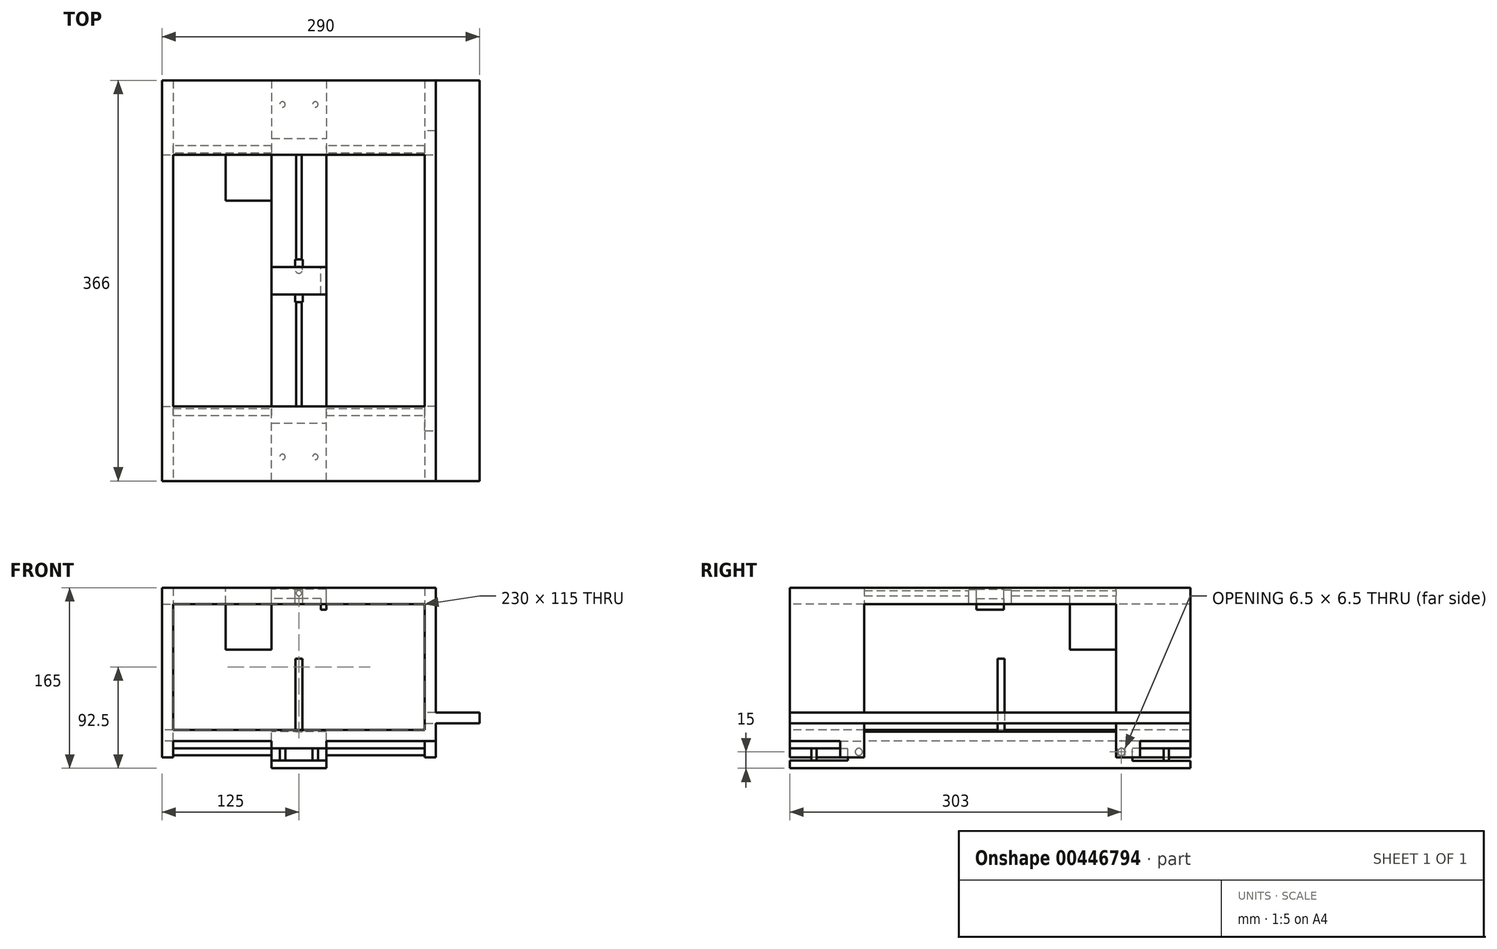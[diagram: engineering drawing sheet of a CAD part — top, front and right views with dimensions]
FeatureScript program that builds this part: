
annotation { "Feature Type Name" : "Feature", "Feature Type Description" : "" }
export const myFeature = defineFeature(function(context is Context, id is Id, definition is map)
    precondition{}
    {
        {
            var Q0;
            Q0=qCreatedBy(makeId("Top.planeOp"),FACE);
            var sketch = newSketch(context, id + "F0", { "sketchPlane" : qUnion([Q0])});
            skLineSegment(sketch, "E0.bottom", {"start": v(-125, 125) * mm, "end": v(125, 125) * mm});
            skLineSegment(sketch, "E0.top", {"start": v(-125, -125) * mm, "end": v(125, -125) * mm});
            skLineSegment(sketch, "E0.left", {"start": v(-125, 125) * mm, "end": v(-125, -125) * mm});
            skLineSegment(sketch, "E0.right", {"start": v(125, 125) * mm, "end": v(125, -125) * mm});
            skSolve(sketch);
        }
        {
            var Q0;
            Q0=qSketchRegion(id+"F0",true);
            extrude(context, id + "F1", {"entities" : qUnion([Q0]), "endBound" : BoundingType.SYMMETRIC, "depth" : 140 * mm});
        }
        {
            var Q0;
            Q0=makeQuery(id+"F1.opExtrude","CAP_FACE",FACE,{"disambiguationData":[OSD([sQuery(id+"F0.wireOp",EDGE,"E0.bottom"),sQuery(id+"F0.wireOp",EDGE,"E0.top"),sQuery(id+"F0.wireOp",EDGE,"E0.left"),sQuery(id+"F0.wireOp",EDGE,"E0.right")])],"isStart":false});
            shell(context, id + "F2", {"entities" : qUnion([Q0]), "thickness" : 10 * mm});
        }
        {
            var Q0;
            Q0=makeQuery(id+"F1.opExtrude","SWEPT_FACE",FACE,{"disambiguationData":[OSD([sQuery(id+"F0.wireOp",EDGE,"E0.top")])]});
            var sketch = newSketch(context, id + "F3", { "sketchPlane" : qUnion([Q0])});
            skLineSegment(sketch, "E1.bottom", {"start": v(-115, 60) * mm, "end": v(115, 60) * mm});
            skLineSegment(sketch, "E1.top", {"start": v(-115, -60) * mm, "end": v(115, -60) * mm});
            skLineSegment(sketch, "E1.left", {"start": v(-115, 60) * mm, "end": v(-115, -60) * mm});
            skLineSegment(sketch, "E1.right", {"start": v(115, 60) * mm, "end": v(115, -60) * mm});
            skSolve(sketch);
        }
        {
            var Q0;
            Q0=makeQuery(id+"F3.imprint","IMPRINT",FACE,{"disambiguationData":[TD([[makeQuery(id+"F3.imprint","IMPRINT",EDGE,{"derivedFrom":sQuery(id+"F3.wireOp",EDGE,"E1.bottom")}),-1.0]])]});
            extrude(context, id + "F4", {"entities" : qUnion([Q0]), "operationType" : NewBodyOperationType.REMOVE, "oppositeDirection" : true, "depth" : 300 * mm});
        }
        {
            var Q0;
            Q0=makeQuery(id+"F1.opExtrude","SWEPT_FACE",FACE,{"disambiguationData":[OSD([sQuery(id+"F0.wireOp",EDGE,"E0.left")])]});
            var sketch = newSketch(context, id + "F5", { "sketchPlane" : qUnion([Q0])});
            skLineSegment(sketch, "E2.bottom", {"start": v(115, 60) * mm, "end": v(-115, 60) * mm});
            skLineSegment(sketch, "E2.top", {"start": v(115, -60) * mm, "end": v(-115, -60) * mm});
            skLineSegment(sketch, "E2.left", {"start": v(115, 60) * mm, "end": v(115, -60) * mm});
            skLineSegment(sketch, "E2.right", {"start": v(-115, 60) * mm, "end": v(-115, -60) * mm});
            skSolve(sketch);
        }
        {
            var Q0;
            Q0=makeQuery(id+"F5.imprint","IMPRINT",FACE,{"disambiguationData":[TD([[makeQuery(id+"F5.imprint","IMPRINT",EDGE,{"derivedFrom":sQuery(id+"F5.wireOp",EDGE,"E2.bottom")}),1.0]])]});
            extrude(context, id + "F6", {"entities" : qUnion([Q0]), "operationType" : NewBodyOperationType.REMOVE, "oppositeDirection" : true, "depth" : 300 * mm});
        }
        {
            var Q0;
            Q0=makeQuery(id+"F6.boolean.opBoolean","MERGE",FACE,{"derivedFrom":[makeQuery(id+"F4.boolean.opBoolean","MERGE",FACE,{"derivedFrom":[makeQuery(id+"F2.opShell","OFFSET_FACE",FACE,{"disambiguationData":[OSD([sQuery(id+"F0.wireOp",EDGE,"E0.bottom"),sQuery(id+"F0.wireOp",EDGE,"E0.top"),sQuery(id+"F0.wireOp",EDGE,"E0.left"),sQuery(id+"F0.wireOp",EDGE,"E0.right")])]}),makeQuery(id+"F4.opExtrude","SWEPT_FACE",FACE,{"disambiguationData":[OSD([sQuery(id+"F3.wireOp",EDGE,"E1.top")])]})]}),makeQuery(id+"F6.opExtrude","SWEPT_FACE",FACE,{"disambiguationData":[OSD([sQuery(id+"F5.wireOp",EDGE,"E2.top")])]})]});
            var sketch = newSketch(context, id + "F7", { "sketchPlane" : qUnion([Q0])});
            skLineSegment(sketch, "E3.bottom", {"start": v(-115, 115) * mm, "end": v(115, 115) * mm});
            skLineSegment(sketch, "E3.top", {"start": v(-115, -115) * mm, "end": v(115, -115) * mm});
            skLineSegment(sketch, "E3.left", {"start": v(-115, 115) * mm, "end": v(-115, -115) * mm});
            skLineSegment(sketch, "E3.right", {"start": v(115, 115) * mm, "end": v(115, -115) * mm});
            skSolve(sketch);
        }
        {
            var Q0;
            Q0=makeQuery(id+"F7.imprint","IMPRINT",FACE,{"disambiguationData":[TD([[makeQuery(id+"F7.imprint","IMPRINT",EDGE,{"derivedFrom":sQuery(id+"F7.wireOp",EDGE,"E3.bottom")}),-1.0]])]});
            extrude(context, id + "F8", {"entities" : qUnion([Q0]), "operationType" : NewBodyOperationType.REMOVE, "oppositeDirection" : true, "depth" : 500 * mm});
        }
        {
            var Q0;
            Q0=makeQuery(id+"F1.opExtrude","CAP_FACE",FACE,{"disambiguationData":[OSD([sQuery(id+"F0.wireOp",EDGE,"E0.bottom"),sQuery(id+"F0.wireOp",EDGE,"E0.top"),sQuery(id+"F0.wireOp",EDGE,"E0.left"),sQuery(id+"F0.wireOp",EDGE,"E0.right")])],"isStart":true});
            var sketch = newSketch(context, id + "F9", { "sketchPlane" : qUnion([Q0])});
            skLineSegment(sketch, "E4.bottom", {"start": v(-125, -125) * mm, "end": v(-115, -125) * mm});
            skLineSegment(sketch, "E4.top", {"start": v(-125, -115) * mm, "end": v(-115, -115) * mm});
            skLineSegment(sketch, "E4.left", {"start": v(-125, -125) * mm, "end": v(-125, -115) * mm});
            skLineSegment(sketch, "E4.right", {"start": v(-115, -125) * mm, "end": v(-115, -115) * mm});
            skLineSegment(sketch, "E5.bottom", {"start": v(-115, 115) * mm, "end": v(-125, 115) * mm});
            skLineSegment(sketch, "E5.top", {"start": v(-115, 125) * mm, "end": v(-125, 125) * mm});
            skLineSegment(sketch, "E5.left", {"start": v(-115, 115) * mm, "end": v(-115, 125) * mm});
            skLineSegment(sketch, "E5.right", {"start": v(-125, 115) * mm, "end": v(-125, 125) * mm});
            skLineSegment(sketch, "E6.bottom", {"start": v(125, -125) * mm, "end": v(115, -125) * mm});
            skLineSegment(sketch, "E6.top", {"start": v(125, -115) * mm, "end": v(115, -115) * mm});
            skLineSegment(sketch, "E6.left", {"start": v(125, -125) * mm, "end": v(125, -115) * mm});
            skLineSegment(sketch, "E6.right", {"start": v(115, -125) * mm, "end": v(115, -115) * mm});
            skLineSegment(sketch, "E7.bottom", {"start": v(125, 125) * mm, "end": v(115, 125) * mm});
            skLineSegment(sketch, "E7.top", {"start": v(125, 115) * mm, "end": v(115, 115) * mm});
            skLineSegment(sketch, "E7.left", {"start": v(125, 125) * mm, "end": v(125, 115) * mm});
            skLineSegment(sketch, "E7.right", {"start": v(115, 125) * mm, "end": v(115, 115) * mm});
            skSolve(sketch);
        }
        {
            var Q0;
            Q0=qSketchRegion(id+"F9",true);
            var Q1;
            Q1=makeQuery(id+"F1.opExtrude","CAP_FACE",FACE,{"disambiguationData":[OSD([sQuery(id+"F0.wireOp",EDGE,"E0.bottom"),sQuery(id+"F0.wireOp",EDGE,"E0.top"),sQuery(id+"F0.wireOp",EDGE,"E0.left"),sQuery(id+"F0.wireOp",EDGE,"E0.right")])],"isStart":false});
            extrude(context, id + "F10", {"entities" : qUnion([Q0, Q1]), "operationType" : NewBodyOperationType.ADD, "depth" : 15 * mm});
        }
        {
            var Q0;
            Q0=makeQuery(id+"F10.boolean.opBoolean","MERGE",FACE,{"derivedFrom":[makeQuery(id+"F1.opExtrude","SWEPT_FACE",FACE,{"disambiguationData":[OSD([sQuery(id+"F0.wireOp",EDGE,"E0.bottom")])]}),makeQuery(id+"F10.opExtrude","SWEPT_FACE",FACE,{"disambiguationData":[OSD([sQuery(id+"F9.wireOp",EDGE,"E4.bottom")])]}),makeQuery(id+"F10.opExtrude","SWEPT_FACE",FACE,{"disambiguationData":[OSD([sQuery(id+"F9.wireOp",EDGE,"E6.bottom")])]})]});
            var sketch = newSketch(context, id + "F11", { "sketchPlane" : qUnion([Q0])});
            skCircle(sketch, "E8", {"center": v(0, 65) * mm, "radius": 2.5 * mm});
            skSolve(sketch);
        }
        {
            var Q0;
            Q0=qSketchRegion(id+"F11",true);
            extrude(context, id + "F12", {"entities" : qUnion([Q0]), "operationType" : NewBodyOperationType.ADD, "oppositeDirection" : true, "depth" : 250 * mm});
        }
        {
            var Q0;
            Q0=qCreatedBy(makeId("Front.planeOp"),FACE);
            var sketch = newSketch(context, id + "F13", { "sketchPlane" : qUnion([Q0])});
            skLineSegment(sketch, "E9.bottom", {"start": v(25, 50) * mm, "end": v(-25, 50) * mm});
            skLineSegment(sketch, "E9.top", {"start": v(25, 68.5) * mm, "end": v(-25, 68.5) * mm});
            skLineSegment(sketch, "E9.left", {"start": v(25, 50) * mm, "end": v(25, 68.5) * mm});
            skLineSegment(sketch, "E9.right", {"start": v(-25, 50) * mm, "end": v(-25, 68.5) * mm});
            skSolve(sketch);
        }
        {
            var Q0;
            Q0=qSketchRegion(id+"F13",true);
            extrude(context, id + "F14", {"entities" : qUnion([Q0]), "operationType" : NewBodyOperationType.ADD, "endBound" : BoundingType.SYMMETRIC, "depth" : 25 * mm});
        }
        {
            var Q0;
            Q0=makeQuery(id+"F14.opExtrude","SWEPT_FACE",FACE,{"disambiguationData":[OSD([sQuery(id+"F13.wireOp",EDGE,"E9.bottom")])]});
            var sketch = newSketch(context, id + "F15", { "sketchPlane" : qUnion([Q0])});
            skLineSegment(sketch, "E10.right", {"start": v(20, 7.5) * mm, "end": v(20, -12.5) * mm});
            skLineSegment(sketch, "E11", {"start": v(20, 7.5) * mm, "end": v(20, 12.5) * mm});
            skLineSegment(sketch, "E12", {"start": v(20, 12.5) * mm, "end": v(25, 12.5) * mm});
            skLineSegment(sketch, "E13", {"start": v(25, 12.5) * mm, "end": v(25, -12.5) * mm});
            skLineSegment(sketch, "E14", {"start": v(25, -12.5) * mm, "end": v(20, -12.5) * mm});
            skSolve(sketch);
        }
        {
            var Q0;
            {var subQ3=sQuery(id+"F15.wireOp",EDGE,"E10.right");Q0=makeQuery(id+"F15.imprint","IMPRINT",FACE,{"disambiguationData":[TD([[makeQuery(id+"F15.imprint","IMPRINT",EDGE,{"derivedFrom":subQ3}),-1.0]])]});}
            extrude(context, id + "F16", {"entities" : qUnion([Q0]), "operationType" : NewBodyOperationType.REMOVE, "oppositeDirection" : true, "depth" : 10 * mm});
        }
        {
            var Q0;
            Q0=qCreatedBy(makeId("Right.planeOp"),FACE);
            var sketch = newSketch(context, id + "F17", { "sketchPlane" : qUnion([Q0])});
            skLineSegment(sketch, "E15.bottom", {"start": v(-12.5, 55) * mm, "end": v(-19.5, 55) * mm});
            skLineSegment(sketch, "E15.top", {"start": v(-12.5, 68) * mm, "end": v(-19.5, 68) * mm});
            skLineSegment(sketch, "E15.left", {"start": v(-12.5, 55) * mm, "end": v(-12.5, 68) * mm});
            skLineSegment(sketch, "E15.right", {"start": v(-19.5, 55) * mm, "end": v(-19.5, 68) * mm});
            skLineSegment(sketch, "E16.bottom", {"start": v(12.5, 55) * mm, "end": v(19.5, 55) * mm});
            skLineSegment(sketch, "E16.top", {"start": v(12.5, 68) * mm, "end": v(19.5, 68) * mm});
            skLineSegment(sketch, "E16.left", {"start": v(12.5, 55) * mm, "end": v(12.5, 68) * mm});
            skLineSegment(sketch, "E16.right", {"start": v(19.5, 55) * mm, "end": v(19.5, 68) * mm});
            skSolve(sketch);
        }
        {
            var Q0;
            Q0=qSketchRegion(id+"F17",true);
            extrude(context, id + "F18", {"entities" : qUnion([Q0]), "operationType" : NewBodyOperationType.ADD, "endBound" : BoundingType.SYMMETRIC, "depth" : 7 * mm});
        }
        {
            var Q0;
            Q0=makeQuery(id+"F10.opExtrude","SWEPT_FACE",FACE,{"disambiguationData":[OSD([sQuery(id+"F9.wireOp",EDGE,"E4.right")])]});
            var sketch = newSketch(context, id + "F19", { "sketchPlane" : qUnion([Q0])});
            skCircle(sketch, "E17", {"center": v(120, -80) * mm, "radius": 3.25 * mm});
            skSolve(sketch);
        }
        {
            var Q0;
            Q0=qSketchRegion(id+"F19",true);
            extrude(context, id + "F20", {"entities" : qUnion([Q0]), "operationType" : NewBodyOperationType.ADD, "depth" : 240 * mm});
        }
        {
            var Q0;
            Q0=qCreatedBy(makeId("Front.planeOp"),FACE);
            var sketch = newSketch(context, id + "F21", { "sketchPlane" : qUnion([Q0])});
            skLineSegment(sketch, "E18.bottom", {"start": v(25, -95) * mm, "end": v(-25, -95) * mm});
            skLineSegment(sketch, "E18.top", {"start": v(25, -61.69) * mm, "end": v(-25, -61.69) * mm});
            skLineSegment(sketch, "E18.left", {"start": v(25, -95) * mm, "end": v(25, -61.69) * mm});
            skLineSegment(sketch, "E18.right", {"start": v(-25, -95) * mm, "end": v(-25, -61.69) * mm});
            skSolve(sketch);
        }
        {
            var Q0;
            Q0=makeQuery(id+"F21.imprint","IMPRINT",FACE,{"disambiguationData":[TD([[makeQuery(id+"F21.imprint","IMPRINT",EDGE,{"derivedFrom":sQuery(id+"F21.wireOp",EDGE,"E18.bottom")}),-1.0]])]});
            extrude(context, id + "F22", {"entities" : qUnion([Q0]), "operationType" : NewBodyOperationType.ADD, "endBound" : BoundingType.SYMMETRIC, "depth" : 230 * mm});
        }
        {
            var Q0;
            Q0=makeQuery(id+"F10.opExtrude","SWEPT_FACE",FACE,{"disambiguationData":[OSD([sQuery(id+"F9.wireOp",EDGE,"E7.right")])]});
            var sketch = newSketch(context, id + "F23", { "sketchPlane" : qUnion([Q0])});
            skCircle(sketch, "E19", {"center": v(120, -80) * mm, "radius": 3.25 * mm});
            skSolve(sketch);
        }
        {
            var Q0;
            Q0=makeQuery(id+"F23.imprint","IMPRINT",FACE,{"disambiguationData":[TD([[makeQuery(id+"F23.imprint","IMPRINT",EDGE,{"derivedFrom":sQuery(id+"F23.wireOp",EDGE,"E19")}),1.0]])]});
            extrude(context, id + "F24", {"entities" : qUnion([Q0]), "operationType" : NewBodyOperationType.ADD, "depth" : 240 * mm});
        }
        {
            var Q0;
            Q0=makeQuery(id+"F22.opExtrude","SWEPT_FACE",FACE,{"disambiguationData":[OSD([sQuery(id+"F21.wireOp",EDGE,"E18.bottom")])]});
            var sketch = newSketch(context, id + "F25", { "sketchPlane" : qUnion([Q0])});
            skCircle(sketch, "E20", {"center": v(0, -10) * mm, "radius": 3.25 * mm});
            skSolve(sketch);
        }
        {
            var Q0;
            Q0=makeQuery(id+"F25.imprint","IMPRINT",FACE,{"disambiguationData":[TD([[makeQuery(id+"F25.imprint","IMPRINT",EDGE,{"derivedFrom":sQuery(id+"F25.wireOp",EDGE,"E20")}),1.0]])]});
            extrude(context, id + "F26", {"entities" : qUnion([Q0]), "operationType" : NewBodyOperationType.ADD, "oppositeDirection" : true, "depth" : 100 * mm});
        }
        {
            var Q0;
            Q0=makeQuery(id+"F1.opExtrude","CAP_FACE",FACE,{"disambiguationData":[OSD([sQuery(id+"F0.wireOp",EDGE,"E0.bottom"),sQuery(id+"F0.wireOp",EDGE,"E0.top"),sQuery(id+"F0.wireOp",EDGE,"E0.left"),sQuery(id+"F0.wireOp",EDGE,"E0.right")])],"isStart":false});
            var sketch = newSketch(context, id + "F27", { "sketchPlane" : qUnion([Q0])});
            skLineSegment(sketch, "E21.0", {"start": v(-25, -12.5) * mm, "end": v(-25, 12.5) * mm});
            skLineSegment(sketch, "E22.0", {"start": v(-25, -115) * mm, "end": v(-25, 115) * mm});
            skLineSegment(sketch, "E23.bottom", {"start": v(-25, 115) * mm, "end": v(-67, 115) * mm});
            skLineSegment(sketch, "E23.top", {"start": v(-25, 73) * mm, "end": v(-67, 73) * mm});
            skLineSegment(sketch, "E23.left", {"start": v(-25, 115) * mm, "end": v(-25, 73) * mm});
            skLineSegment(sketch, "E23.right", {"start": v(-67, 115) * mm, "end": v(-67, 73) * mm});
            skSolve(sketch);
        }
        {
            var Q0;
            Q0=makeQuery(id+"F27.imprint","IMPRINT",FACE,{"disambiguationData":[TD([[makeQuery(id+"F27.imprint","IMPRINT",EDGE,{"derivedFrom":sQuery(id+"F27.wireOp",EDGE,"E23.bottom")}),-1.0]])]});
            extrude(context, id + "F28", {"entities" : qUnion([Q0]), "oppositeDirection" : true, "depth" : 56.5 * mm});
        }
        {
            var Q0;
            {var subQ0=sQuery(id+"F0.wireOp",EDGE,"E0.bottom");Q0=makeQuery(id+"F10.boolean.opBoolean","MERGE",FACE,{"derivedFrom":[makeQuery(id+"F1.opExtrude","SWEPT_FACE",FACE,{"disambiguationData":[OSD([subQ0])]}),makeQuery(id+"F10.opExtrude","SWEPT_FACE",FACE,{"disambiguationData":[OSD([subQ0]),TDD([makeQuery(id+"F1.opExtrude","CAP_EDGE",EDGE,{"disambiguationData":[OSD([subQ0])],"isStart":false})])]}),makeQuery(id+"F10.opExtrude","SWEPT_FACE",FACE,{"disambiguationData":[OSD([sQuery(id+"F9.wireOp",EDGE,"E4.bottom")])]}),makeQuery(id+"F10.opExtrude","SWEPT_FACE",FACE,{"disambiguationData":[OSD([sQuery(id+"F9.wireOp",EDGE,"E6.bottom")])]})]});}
            var sketch = newSketch(context, id + "F29", { "sketchPlane" : qUnion([Q0])});
            skLineSegment(sketch, "E24.0.0", {"start": v(-115, -70) * mm, "end": v(115, -70) * mm});
            skLineSegment(sketch, "E24.0.1", {"start": v(115, -70) * mm, "end": v(115, -85) * mm});
            skLineSegment(sketch, "E24.0.2", {"start": v(115, -85) * mm, "end": v(125, -85) * mm});
            skLineSegment(sketch, "E24.0.3", {"start": v(125, -85) * mm, "end": v(125, 70) * mm});
            skLineSegment(sketch, "E24.0.4", {"start": v(125, 70) * mm, "end": v(-125, 70) * mm});
            skLineSegment(sketch, "E24.0.5", {"start": v(-125, 70) * mm, "end": v(-125, -85) * mm});
            skLineSegment(sketch, "E24.0.6", {"start": v(-125, -85) * mm, "end": v(-115, -85) * mm});
            skLineSegment(sketch, "E24.0.7", {"start": v(-115, -85) * mm, "end": v(-115, -70) * mm});
            skSolve(sketch);
        }
        {
            var Q0;
            Q0=makeQuery(id+"F29.imprint","IMPRINT",FACE,{"disambiguationData":[TD([[makeQuery(id+"F29.imprint","IMPRINT",EDGE,{"derivedFrom":sQuery(id+"F29.wireOp",EDGE,"E24.0.0")}),-1.0]])]});
            extrude(context, id + "F30", {"entities" : qUnion([Q0]), "operationType" : NewBodyOperationType.ADD, "depth" : 58 * mm});
        }
        {
            var Q0;
            {var subQ0=sQuery(id+"F0.wireOp",EDGE,"E0.top");Q0=makeQuery(id+"F10.boolean.opBoolean","MERGE",FACE,{"derivedFrom":[makeQuery(id+"F1.opExtrude","SWEPT_FACE",FACE,{"disambiguationData":[OSD([subQ0])]}),makeQuery(id+"F10.opExtrude","SWEPT_FACE",FACE,{"disambiguationData":[OSD([subQ0]),TDD([makeQuery(id+"F1.opExtrude","CAP_EDGE",EDGE,{"disambiguationData":[OSD([subQ0])],"isStart":false})])]}),makeQuery(id+"F10.opExtrude","SWEPT_FACE",FACE,{"disambiguationData":[OSD([sQuery(id+"F9.wireOp",EDGE,"E5.top")])]}),makeQuery(id+"F10.opExtrude","SWEPT_FACE",FACE,{"disambiguationData":[OSD([sQuery(id+"F9.wireOp",EDGE,"E7.bottom")])]})]});}
            var sketch = newSketch(context, id + "F31", { "sketchPlane" : qUnion([Q0])});
            skPoint(sketch, "E25.0", {"position": v(115, -70) * mm});
            skPoint(sketch, "E25.1", {"position": v(115, -60) * mm});
            skSolve(sketch);
        }
        {
            var Q0;
            {var subQ0=sQuery(id+"F0.wireOp",EDGE,"E0.top");var subQ3=makeQuery(id+"F1.opExtrude","CAP_EDGE",EDGE,{"disambiguationData":[OSD([subQ0])],"isStart":false});Q0=makeQuery(id+"F31.imprint","IMPRINT",FACE,{"disambiguationData":[TD([[makeQuery(id+"F31.imprint","IMPRINT",EDGE,{"derivedFrom":subQ3}),-1.0]])]});}
            extrude(context, id + "F32", {"entities" : qUnion([Q0]), "operationType" : NewBodyOperationType.ADD, "depth" : 58 * mm});
        }
        {
            var Q0;
            {var subQ0=sQuery(id+"F21.wireOp",EDGE,"E18.bottom");var subQ1=sQuery(id+"F21.wireOp",EDGE,"E18.left");var subQ2=sQuery(id+"F21.wireOp",EDGE,"E18.right");Q0=makeQuery(id+"F22.boolean.opBoolean","SPLIT",FACE,{"disambiguationData":[TD([makeQuery(id+"F22.opExtrude","SWEPT_FACE",FACE,{"disambiguationData":[OSD([subQ0])]})])],"derivedFrom":makeQuery(id+"F22.opExtrude","CAP_FACE",FACE,{"disambiguationData":[OSD([subQ0,sQuery(id+"F21.wireOp",EDGE,"E18.top"),subQ1,subQ2])],"isStart":true})});}
            var sketch = newSketch(context, id + "F33", { "sketchPlane" : qUnion([Q0])});
            skLineSegment(sketch, "E26.0.0", {"start": v(25, -95) * mm, "end": v(25, -70) * mm});
            skLineSegment(sketch, "E26.0.1", {"start": v(25, -70) * mm, "end": v(-25, -70) * mm});
            skLineSegment(sketch, "E26.0.2", {"start": v(-25, -70) * mm, "end": v(-25, -95) * mm});
            skLineSegment(sketch, "E26.0.3", {"start": v(-25, -95) * mm, "end": v(25, -95) * mm});
            skSolve(sketch);
        }
        {
            var Q0;
            Q0=qSketchRegion(id+"F33",true);
            extrude(context, id + "F34", {"entities" : qUnion([Q0]), "operationType" : NewBodyOperationType.ADD, "depth" : 15 * mm});
        }
        {
            var Q0;
            Q0=makeQuery(id+"F34.opExtrude","CAP_FACE",FACE,{"disambiguationData":[OSD([sQuery(id+"F33.wireOp",EDGE,"E26.0.0"),sQuery(id+"F33.wireOp",EDGE,"E26.0.1"),sQuery(id+"F33.wireOp",EDGE,"E26.0.2"),sQuery(id+"F33.wireOp",EDGE,"E26.0.3")])],"isStart":false});
            var sketch = newSketch(context, id + "F35", { "sketchPlane" : qUnion([Q0])});
            skLineSegment(sketch, "E27.bottom", {"start": v(25, -95) * mm, "end": v(-25, -95) * mm});
            skLineSegment(sketch, "E27.top", {"start": v(25, -88.07) * mm, "end": v(-25, -88.07) * mm});
            skLineSegment(sketch, "E27.left", {"start": v(25, -95) * mm, "end": v(25, -88.07) * mm});
            skLineSegment(sketch, "E27.right", {"start": v(-25, -95) * mm, "end": v(-25, -88.07) * mm});
            skLineSegment(sketch, "E28.bottom", {"start": v(25, -70) * mm, "end": v(-25, -70) * mm});
            skLineSegment(sketch, "E28.top", {"start": v(25, -76.65) * mm, "end": v(-25, -76.65) * mm});
            skLineSegment(sketch, "E28.left", {"start": v(25, -70) * mm, "end": v(25, -76.65) * mm});
            skLineSegment(sketch, "E28.right", {"start": v(-25, -70) * mm, "end": v(-25, -76.65) * mm});
            skSolve(sketch);
        }
        {
            var Q0;
            Q0=makeQuery(id+"F35.imprint","IMPRINT",FACE,{"disambiguationData":[TD([[makeQuery(id+"F35.imprint","IMPRINT",EDGE,{"derivedFrom":sQuery(id+"F35.wireOp",EDGE,"E27.bottom")}),1.0]])]});
            var Q1;
            Q1=makeQuery(id+"F35.imprint","IMPRINT",FACE,{"disambiguationData":[TD([[makeQuery(id+"F35.imprint","IMPRINT",EDGE,{"derivedFrom":sQuery(id+"F35.wireOp",EDGE,"E28.bottom")}),1.0]])]});
            var Q2;
            Q2=makeQuery(id+"F30.opExtrude","CAP_FACE",FACE,{"disambiguationData":[OSD([sQuery(id+"F0.wireOp",EDGE,"E0.bottom"),sQuery(id+"F3.wireOp",EDGE,"E1.top"),sQuery(id+"F3.wireOp",EDGE,"E1.left"),sQuery(id+"F3.wireOp",EDGE,"E1.right"),sQuery(id+"F29.wireOp",EDGE,"E24.0.0"),sQuery(id+"F29.wireOp",EDGE,"E24.0.1"),sQuery(id+"F29.wireOp",EDGE,"E24.0.2"),sQuery(id+"F29.wireOp",EDGE,"E24.0.3"),sQuery(id+"F29.wireOp",EDGE,"E24.0.4"),sQuery(id+"F29.wireOp",EDGE,"E24.0.5"),sQuery(id+"F29.wireOp",EDGE,"E24.0.6"),sQuery(id+"F29.wireOp",EDGE,"E24.0.7")])],"isStart":false});
            extrude(context, id + "F36", {"entities" : qUnion([Q0, Q1]), "operationType" : NewBodyOperationType.ADD, "endBound" : BoundingType.UP_TO_SURFACE, "endBoundEntityFace" : qUnion([Q2]), "depth" : 25 * mm});
        }
        {
            var Q0;
            Q0=makeQuery(id+"F36.opExtrude","SWEPT_FACE",FACE,{"disambiguationData":[OSD([sQuery(id+"F35.wireOp",EDGE,"E28.top")])]});
            var sketch = newSketch(context, id + "F37", { "sketchPlane" : qUnion([Q0])});
            skCircle(sketch, "E29", {"center": v(-15, -161) * mm, "radius": 2.5 * mm});
            skCircle(sketch, "E30", {"center": v(15, -161) * mm, "radius": 2.5 * mm});
            skSolve(sketch);
        }
        {
            var Q0;
            Q0=makeQuery(id+"F37.imprint","IMPRINT",FACE,{"disambiguationData":[TD([[makeQuery(id+"F37.imprint","IMPRINT",EDGE,{"derivedFrom":sQuery(id+"F37.wireOp",EDGE,"E29")}),1.0]])]});
            var Q1;
            Q1=makeQuery(id+"F37.imprint","IMPRINT",FACE,{"disambiguationData":[TD([[makeQuery(id+"F37.imprint","IMPRINT",EDGE,{"derivedFrom":sQuery(id+"F37.wireOp",EDGE,"E30")}),1.0]])]});
            extrude(context, id + "F38", {"entities" : qUnion([Q0, Q1]), "operationType" : NewBodyOperationType.ADD, "endBound" : BoundingType.UP_TO_NEXT, "depth" : 25 * mm});
        }
        {
            var Q0;
            {var subQ0=sQuery(id+"F0.wireOp",EDGE,"E0.right");var subQ1=makeQuery(id+"F1.opExtrude","CAP_FACE",FACE,{"disambiguationData":[OSD([sQuery(id+"F0.wireOp",EDGE,"E0.bottom"),sQuery(id+"F0.wireOp",EDGE,"E0.top"),sQuery(id+"F0.wireOp",EDGE,"E0.left"),subQ0])],"isStart":true});Q0=makeQuery(id+"F10.boolean.opBoolean","SPLIT",FACE,{"disambiguationData":[TD([makeQuery(id+"F1.opExtrude","SWEPT_FACE",FACE,{"disambiguationData":[OSD([subQ0])]})])],"derivedFrom":subQ1});}
            var sketch = newSketch(context, id + "F39", { "sketchPlane" : qUnion([Q0])});
            skLineSegment(sketch, "E31.bottom", {"start": v(115, -115) * mm, "end": v(125, -115) * mm});
            skLineSegment(sketch, "E31.top", {"start": v(115, 115) * mm, "end": v(125, 115) * mm});
            skLineSegment(sketch, "E31.left", {"start": v(115, -115) * mm, "end": v(115, 115) * mm});
            skLineSegment(sketch, "E31.right", {"start": v(125, -115) * mm, "end": v(125, 115) * mm});
            skSolve(sketch);
        }
        {
            var Q0;
            Q0=makeQuery(id+"F39.imprint","IMPRINT",FACE,{"disambiguationData":[TD([[makeQuery(id+"F39.imprint","IMPRINT",EDGE,{"derivedFrom":sQuery(id+"F39.wireOp",EDGE,"E31.bottom")}),-1.0]])]});
            extrude(context, id + "F40", {"entities" : qUnion([Q0]), "operationType" : NewBodyOperationType.REMOVE, "oppositeDirection" : true, "depth" : 25 * mm});
        }
        {
            var Q0;
            {var subQ0=sQuery(id+"F0.wireOp",EDGE,"E0.right");Q0=makeQuery(id+"F40.boolean.opBoolean","MERGE",FACE,{"derivedFrom":[makeQuery(id+"F10.opExtrude","SWEPT_FACE",FACE,{"disambiguationData":[OSD([sQuery(id+"F9.wireOp",EDGE,"E6.top")])]}),makeQuery(id+"F6.boolean.opBoolean","COPY",FACE,{"disambiguationData":[TD([makeQuery(id+"F1.opExtrude","SWEPT_FACE",FACE,{"disambiguationData":[OSD([subQ0])]})])],"derivedFrom":makeQuery(id+"F6.opExtrude","SWEPT_FACE",FACE,{"disambiguationData":[OSD([sQuery(id+"F5.wireOp",EDGE,"E2.right")])]})}),makeQuery(id+"F8.boolean.opBoolean","COPY",FACE,{"derivedFrom":makeQuery(id+"F8.opExtrude","SWEPT_FACE",FACE,{"disambiguationData":[OSD([sQuery(id+"F7.wireOp",EDGE,"E3.bottom")])]})}),makeQuery(id+"F40.opExtrude","SWEPT_FACE",FACE,{"disambiguationData":[OSD([sQuery(id+"F39.wireOp",EDGE,"E31.bottom")])]})]});}
            var sketch = newSketch(context, id + "F41", { "sketchPlane" : qUnion([Q0])});
            skLineSegment(sketch, "E32.bottom", {"start": v(115, -54) * mm, "end": v(165, -54) * mm});
            skLineSegment(sketch, "E32.top", {"start": v(115, -44) * mm, "end": v(165, -44) * mm});
            skLineSegment(sketch, "E32.left", {"start": v(115, -54) * mm, "end": v(115, -44) * mm});
            skLineSegment(sketch, "E32.right", {"start": v(165, -54) * mm, "end": v(165, -44) * mm});
            skSolve(sketch);
        }
        {
            var Q0;
            {var subQ0=sQuery(id+"F41.wireOp",EDGE,"E32.right");Q0=makeQuery(id+"F41.imprint","IMPRINT",FACE,{"disambiguationData":[TD([[makeQuery(id+"F41.imprint","IMPRINT",EDGE,{"derivedFrom":subQ0}),1.0]])]});}
            var Q1;
            {var subQ0=sQuery(id+"F41.wireOp",EDGE,"E32.left");Q1=makeQuery(id+"F41.imprint","IMPRINT",FACE,{"disambiguationData":[TD([[makeQuery(id+"F41.imprint","IMPRINT",EDGE,{"derivedFrom":subQ0}),-1.0]])]});}
            var Q2;
            {var subQ2=sQuery(id+"F0.wireOp",EDGE,"E0.right");Q2=makeQuery(id+"F40.boolean.opBoolean","MERGE",FACE,{"derivedFrom":[makeQuery(id+"F10.opExtrude","SWEPT_FACE",FACE,{"disambiguationData":[OSD([sQuery(id+"F9.wireOp",EDGE,"E7.top")])]}),makeQuery(id+"F6.boolean.opBoolean","COPY",FACE,{"disambiguationData":[TD([makeQuery(id+"F1.opExtrude","SWEPT_FACE",FACE,{"disambiguationData":[OSD([subQ2])]})])],"derivedFrom":makeQuery(id+"F6.opExtrude","SWEPT_FACE",FACE,{"disambiguationData":[OSD([sQuery(id+"F5.wireOp",EDGE,"E2.left")])]})}),makeQuery(id+"F8.boolean.opBoolean","COPY",FACE,{"derivedFrom":makeQuery(id+"F8.opExtrude","SWEPT_FACE",FACE,{"disambiguationData":[OSD([sQuery(id+"F7.wireOp",EDGE,"E3.top")])]})}),makeQuery(id+"F40.opExtrude","SWEPT_FACE",FACE,{"disambiguationData":[OSD([sQuery(id+"F39.wireOp",EDGE,"E31.top")])]})]});}
            extrude(context, id + "F42", {"entities" : qUnion([Q0, Q1]), "operationType" : NewBodyOperationType.ADD, "endBound" : BoundingType.UP_TO_SURFACE, "endBoundEntityFace" : qUnion([Q2]), "depth" : 211 * mm});
        }
        {
            var Q0;
            Q0=makeQuery(id+"F42.opExtrude","CAP_FACE",FACE,{"disambiguationData":[OSD([sQuery(id+"F41.wireOp",EDGE,"E32.bottom"),sQuery(id+"F41.wireOp",EDGE,"E32.top"),sQuery(id+"F41.wireOp",EDGE,"E32.left"),sQuery(id+"F41.wireOp",EDGE,"E32.right")])],"isStart":true});
            var sketch = newSketch(context, id + "F43", { "sketchPlane" : qUnion([Q0])});
            skLineSegment(sketch, "E33.bottom", {"start": v(-165, -54) * mm, "end": v(-125, -54) * mm});
            skLineSegment(sketch, "E33.top", {"start": v(-165, -44) * mm, "end": v(-125, -44) * mm});
            skLineSegment(sketch, "E33.left", {"start": v(-165, -54) * mm, "end": v(-165, -44) * mm});
            skLineSegment(sketch, "E33.right", {"start": v(-125, -54) * mm, "end": v(-125, -44) * mm});
            skSolve(sketch);
        }
        {
            var Q0;
            Q0=makeQuery(id+"F43.imprint","IMPRINT",FACE,{"disambiguationData":[TD([[makeQuery(id+"F43.imprint","IMPRINT",EDGE,{"derivedFrom":sQuery(id+"F43.wireOp",EDGE,"E33.bottom")}),-1.0]])]});
            var Q1;
            Q1=makeQuery(id+"F36.boolean.opBoolean","MERGE",FACE,{"derivedFrom":[makeQuery(id+"F30.opExtrude","CAP_FACE",FACE,{"disambiguationData":[OSD([sQuery(id+"F0.wireOp",EDGE,"E0.bottom"),sQuery(id+"F3.wireOp",EDGE,"E1.top"),sQuery(id+"F3.wireOp",EDGE,"E1.left"),sQuery(id+"F3.wireOp",EDGE,"E1.right"),sQuery(id+"F29.wireOp",EDGE,"E24.0.0"),sQuery(id+"F29.wireOp",EDGE,"E24.0.1"),sQuery(id+"F29.wireOp",EDGE,"E24.0.2"),sQuery(id+"F29.wireOp",EDGE,"E24.0.3"),sQuery(id+"F29.wireOp",EDGE,"E24.0.4"),sQuery(id+"F29.wireOp",EDGE,"E24.0.5"),sQuery(id+"F29.wireOp",EDGE,"E24.0.6"),sQuery(id+"F29.wireOp",EDGE,"E24.0.7")])],"isStart":false}),makeQuery(id+"F36.opExtrude","CAP_FACE",FACE,{"disambiguationData":[OSD([sQuery(id+"F35.wireOp",EDGE,"E28.bottom"),sQuery(id+"F35.wireOp",EDGE,"E28.top"),sQuery(id+"F35.wireOp",EDGE,"E28.left"),sQuery(id+"F35.wireOp",EDGE,"E28.right")])],"isStart":false})]});
            extrude(context, id + "F44", {"entities" : qUnion([Q0]), "operationType" : NewBodyOperationType.ADD, "endBound" : BoundingType.UP_TO_SURFACE, "endBoundEntityFace" : qUnion([Q1]), "depth" : 25 * mm});
        }
        {
            var Q0;
            Q0=makeQuery(id+"F30.boolean.opBoolean","MERGE",FACE,{"derivedFrom":[makeQuery(id+"F10.opExtrude","SWEPT_FACE",FACE,{"disambiguationData":[OSD([sQuery(id+"F9.wireOp",EDGE,"E6.right")])]}),makeQuery(id+"F30.opExtrude","SWEPT_FACE",FACE,{"disambiguationData":[OSD([sQuery(id+"F29.wireOp",EDGE,"E24.0.7")])]})]});
            var sketch = newSketch(context, id + "F45", { "sketchPlane" : qUnion([Q0])});
            skLineSegment(sketch, "E34.bottom", {"start": v(-183, -70) * mm, "end": v(-137.06, -70) * mm});
            skLineSegment(sketch, "E34.top", {"start": v(-183, -85) * mm, "end": v(-137.06, -85) * mm});
            skLineSegment(sketch, "E34.left", {"start": v(-183, -70) * mm, "end": v(-183, -85) * mm});
            skLineSegment(sketch, "E34.right", {"start": v(-137.06, -70) * mm, "end": v(-137.06, -85) * mm});
            skSolve(sketch);
        }
        {
            var Q0;
            Q0=makeQuery(id+"F45.imprint","IMPRINT",FACE,{"disambiguationData":[TD([[makeQuery(id+"F45.imprint","IMPRINT",EDGE,{"derivedFrom":sQuery(id+"F45.wireOp",EDGE,"E34.bottom")}),-1.0]])]});
            extrude(context, id + "F46", {"entities" : qUnion([Q0]), "operationType" : NewBodyOperationType.REMOVE, "oppositeDirection" : true, "depth" : 25 * mm});
        }
        {
            var Q0;
            Q0=makeQuery(id+"F42.opExtrude","CAP_FACE",FACE,{"disambiguationData":[OSD([sQuery(id+"F41.wireOp",EDGE,"E32.bottom"),sQuery(id+"F41.wireOp",EDGE,"E32.top"),sQuery(id+"F41.wireOp",EDGE,"E32.left"),sQuery(id+"F41.wireOp",EDGE,"E32.right")])],"isStart":false});
            var Q1;
            Q1=makeQuery(id+"F32.opExtrude","CAP_FACE",FACE,{"disambiguationData":[OSD([sQuery(id+"F0.wireOp",EDGE,"E0.top"),sQuery(id+"F0.wireOp",EDGE,"E0.left"),sQuery(id+"F0.wireOp",EDGE,"E0.right"),sQuery(id+"F3.wireOp",EDGE,"E1.top"),sQuery(id+"F3.wireOp",EDGE,"E1.left"),sQuery(id+"F3.wireOp",EDGE,"E1.right"),sQuery(id+"F9.wireOp",EDGE,"E5.top"),sQuery(id+"F9.wireOp",EDGE,"E5.left"),sQuery(id+"F9.wireOp",EDGE,"E5.right"),sQuery(id+"F9.wireOp",EDGE,"E7.bottom"),sQuery(id+"F9.wireOp",EDGE,"E7.left"),sQuery(id+"F9.wireOp",EDGE,"E7.right")])],"isStart":false});
            extrude(context, id + "F47", {"entities" : qUnion([Q0]), "operationType" : NewBodyOperationType.ADD, "endBound" : BoundingType.UP_TO_SURFACE, "endBoundEntityFace" : qUnion([Q1]), "depth" : 25 * mm});
        }
        {
            var Q0;
            {var subQ1=sQuery(id+"F29.wireOp",EDGE,"E24.0.6");var subQ2=sQuery(id+"F9.wireOp",EDGE,"E6.left");var subQ4=sQuery(id+"F0.wireOp",EDGE,"E0.right");var subQ6=sQuery(id+"F0.wireOp",EDGE,"E0.top");var subQ8=makeQuery(id+"F1.opExtrude","SWEPT_FACE",FACE,{"disambiguationData":[OSD([subQ4])]});var subQ13=sQuery(id+"F29.wireOp",EDGE,"E24.0.5");var subQ14=sQuery(id+"F9.wireOp",EDGE,"E7.left");Q0=makeQuery(id+"F44.boolean.opBoolean","SPLIT",FACE,{"disambiguationData":[TD([makeQuery(id+"F30.opExtrude","SWEPT_FACE",FACE,{"disambiguationData":[OSD([subQ1])]})])],"derivedFrom":makeQuery(id+"F32.boolean.opBoolean","MERGE",FACE,{"derivedFrom":[makeQuery(id+"F30.boolean.opBoolean","MERGE",FACE,{"derivedFrom":[makeQuery(id+"F10.boolean.opBoolean","MERGE",FACE,{"derivedFrom":[subQ8,makeQuery(id+"F10.opExtrude","SWEPT_FACE",FACE,{"disambiguationData":[OSD([subQ4]),TDD([makeQuery(id+"F1.opExtrude","CAP_EDGE",EDGE,{"disambiguationData":[OSD([subQ4])],"isStart":false})])]}),makeQuery(id+"F10.opExtrude","SWEPT_FACE",FACE,{"disambiguationData":[OSD([subQ2])]}),makeQuery(id+"F10.opExtrude","SWEPT_FACE",FACE,{"disambiguationData":[OSD([subQ14])]})]}),makeQuery(id+"F30.opExtrude","SWEPT_FACE",FACE,{"disambiguationData":[OSD([subQ13])]})]}),makeQuery(id+"F32.opExtrude","SWEPT_FACE",FACE,{"disambiguationData":[OSD([subQ6,subQ4,sQuery(id+"F9.wireOp",EDGE,"E7.bottom"),subQ14])]})]})});}
            var sketch = newSketch(context, id + "F48", { "sketchPlane" : qUnion([Q0])});
            skLineSegment(sketch, "E35.0", {"start": v(-115, -85) * mm, "end": v(-183, -85) * mm});
            skPoint(sketch, "E36.0", {"position": v(-115, -69.5) * mm});
            skLineSegment(sketch, "E37", {"start": v(-137.06, -85) * mm, "end": v(-137.06, -70) * mm});
            skLineSegment(sketch, "E38.0", {"start": v(137.06, -70) * mm, "end": v(183, -70) * mm});
            skLineSegment(sketch, "E39.0", {"start": v(137.06, -85) * mm, "end": v(115, -85) * mm});
            skLineSegment(sketch, "E40.0", {"start": v(115, -85) * mm, "end": v(115, -54) * mm});
            skLineSegment(sketch, "E41", {"start": v(-183, -85) * mm, "end": v(-183, -70) * mm});
            skLineSegment(sketch, "E42", {"start": v(-183, -70) * mm, "end": v(-137.06, -70) * mm});
            skSolve(sketch);
        }
        {
            var Q0;
            {var subQ2=sQuery(id+"F48.wireOp",EDGE,"E37");Q0=makeQuery(id+"F48.imprint","IMPRINT",FACE,{"disambiguationData":[TD([[makeQuery(id+"F48.imprint","IMPRINT",EDGE,{"derivedFrom":subQ2}),1.0]])]});}
            extrude(context, id + "F49", {"entities" : qUnion([Q0]), "operationType" : NewBodyOperationType.REMOVE, "oppositeDirection" : true, "depth" : 25 * mm});
        }
        {
            var Q0;
            Q0=makeQuery(id+"F22.opExtrude","CAP_FACE",FACE,{"disambiguationData":[OSD([sQuery(id+"F21.wireOp",EDGE,"E18.bottom"),sQuery(id+"F21.wireOp",EDGE,"E18.top"),sQuery(id+"F21.wireOp",EDGE,"E18.left"),sQuery(id+"F21.wireOp",EDGE,"E18.right")])],"isStart":false});
            var Q1;
            Q1=makeQuery(id+"F47.boolean.opBoolean","MERGE",FACE,{"derivedFrom":[makeQuery(id+"F32.opExtrude","CAP_FACE",FACE,{"disambiguationData":[OSD([sQuery(id+"F0.wireOp",EDGE,"E0.top"),sQuery(id+"F0.wireOp",EDGE,"E0.left"),sQuery(id+"F0.wireOp",EDGE,"E0.right"),sQuery(id+"F3.wireOp",EDGE,"E1.top"),sQuery(id+"F3.wireOp",EDGE,"E1.left"),sQuery(id+"F3.wireOp",EDGE,"E1.right"),sQuery(id+"F9.wireOp",EDGE,"E5.top"),sQuery(id+"F9.wireOp",EDGE,"E5.left"),sQuery(id+"F9.wireOp",EDGE,"E5.right"),sQuery(id+"F9.wireOp",EDGE,"E7.bottom"),sQuery(id+"F9.wireOp",EDGE,"E7.left"),sQuery(id+"F9.wireOp",EDGE,"E7.right")])],"isStart":false}),makeQuery(id+"F47.opExtrude","CAP_FACE",FACE,{"disambiguationData":[OSD([sQuery(id+"F41.wireOp",EDGE,"E32.bottom"),sQuery(id+"F41.wireOp",EDGE,"E32.top"),sQuery(id+"F41.wireOp",EDGE,"E32.left"),sQuery(id+"F41.wireOp",EDGE,"E32.right")])],"isStart":false})]});
            extrude(context, id + "F50", {"entities" : qUnion([Q0]), "operationType" : NewBodyOperationType.ADD, "endBound" : BoundingType.UP_TO_SURFACE, "endBoundEntityFace" : qUnion([Q1]), "depth" : 25 * mm});
        }
        {
            var Q0;
            {var subQ0=sQuery(id+"F21.wireOp",EDGE,"E18.left");Q0=makeQuery(id+"F50.boolean.opBoolean","MERGE",FACE,{"derivedFrom":[makeQuery(id+"F36.boolean.opBoolean","MERGE",FACE,{"derivedFrom":[makeQuery(id+"F34.boolean.opBoolean","MERGE",FACE,{"derivedFrom":[makeQuery(id+"F22.opExtrude","SWEPT_FACE",FACE,{"disambiguationData":[OSD([subQ0])]}),makeQuery(id+"F34.opExtrude","SWEPT_FACE",FACE,{"disambiguationData":[OSD([sQuery(id+"F33.wireOp",EDGE,"E26.0.2")])]})]}),makeQuery(id+"F36.opExtrude","SWEPT_FACE",FACE,{"disambiguationData":[OSD([sQuery(id+"F35.wireOp",EDGE,"E27.right")])]}),makeQuery(id+"F36.opExtrude","SWEPT_FACE",FACE,{"disambiguationData":[OSD([sQuery(id+"F35.wireOp",EDGE,"E28.right")])]})]}),makeQuery(id+"F50.opExtrude","SWEPT_FACE",FACE,{"disambiguationData":[OSD([subQ0])]})]});}
            var sketch = newSketch(context, id + "F51", { "sketchPlane" : qUnion([Q0])});
            skLineSegment(sketch, "E43.0", {"start": v(130, -88.07) * mm, "end": v(130, -76.65) * mm});
            skLineSegment(sketch, "E44.0", {"start": v(183, -95) * mm, "end": v(183, -88.07) * mm});
            skLineSegment(sketch, "E45.0", {"start": v(183, -76.65) * mm, "end": v(183, -70) * mm});
            skLineSegment(sketch, "E46.bottom", {"start": v(-183, -88) * mm, "end": v(-130, -88) * mm});
            skLineSegment(sketch, "E46.top", {"start": v(-183, -76.7) * mm, "end": v(-130, -76.7) * mm});
            skLineSegment(sketch, "E46.left", {"start": v(-183, -88) * mm, "end": v(-183, -76.7) * mm});
            skLineSegment(sketch, "E46.right", {"start": v(-130, -88) * mm, "end": v(-130, -76.7) * mm});
            skSolve(sketch);
        }
        {
            var Q0;
            Q0=makeQuery(id+"F51.imprint","IMPRINT",FACE,{"disambiguationData":[TD([[makeQuery(id+"F51.imprint","IMPRINT",EDGE,{"derivedFrom":sQuery(id+"F51.wireOp",EDGE,"E46.bottom")}),1.0]])]});
            extrude(context, id + "F52", {"entities" : qUnion([Q0]), "operationType" : NewBodyOperationType.REMOVE, "oppositeDirection" : true, "depth" : 50 * mm});
        }
        {
            var Q0;
            Q0=makeQuery(id+"F52.boolean.opBoolean","COPY",FACE,{"derivedFrom":makeQuery(id+"F52.opExtrude","SWEPT_FACE",FACE,{"disambiguationData":[OSD([sQuery(id+"F51.wireOp",EDGE,"E46.top")])]})});
            var sketch = newSketch(context, id + "F53", { "sketchPlane" : qUnion([Q0])});
            skCircle(sketch, "E47", {"center": v(15, 161) * mm, "radius": 2.5 * mm});
            skCircle(sketch, "E48", {"center": v(-15, 161) * mm, "radius": 2.5 * mm});
            skSolve(sketch);
        }
        {
            var Q0;
            Q0=makeQuery(id+"F53.imprint","IMPRINT",FACE,{"disambiguationData":[TD([[makeQuery(id+"F53.imprint","IMPRINT",EDGE,{"derivedFrom":sQuery(id+"F53.wireOp",EDGE,"E47")}),1.0]])]});
            var Q1;
            Q1=makeQuery(id+"F53.imprint","IMPRINT",FACE,{"disambiguationData":[TD([[makeQuery(id+"F53.imprint","IMPRINT",EDGE,{"derivedFrom":sQuery(id+"F53.wireOp",EDGE,"E48")}),1.0]])]});
            var Q2;
            {var subQ0=sQuery(id+"F21.wireOp",EDGE,"E18.bottom");Q2=makeQuery(id+"F50.boolean.opBoolean","MERGE",FACE,{"derivedFrom":[makeQuery(id+"F36.boolean.opBoolean","MERGE",FACE,{"derivedFrom":[makeQuery(id+"F34.boolean.opBoolean","MERGE",FACE,{"derivedFrom":[makeQuery(id+"F22.opExtrude","SWEPT_FACE",FACE,{"disambiguationData":[OSD([subQ0])]}),makeQuery(id+"F34.opExtrude","SWEPT_FACE",FACE,{"disambiguationData":[OSD([sQuery(id+"F33.wireOp",EDGE,"E26.0.3")])]})]}),makeQuery(id+"F36.opExtrude","SWEPT_FACE",FACE,{"disambiguationData":[OSD([sQuery(id+"F35.wireOp",EDGE,"E27.bottom")])]})]}),makeQuery(id+"F50.opExtrude","SWEPT_FACE",FACE,{"disambiguationData":[OSD([subQ0])]})]});}
            extrude(context, id + "F54", {"entities" : qUnion([Q0, Q1]), "operationType" : NewBodyOperationType.ADD, "endBound" : BoundingType.UP_TO_SURFACE, "endBoundEntityFace" : qUnion([Q2]), "depth" : 25 * mm});
        }
    });
